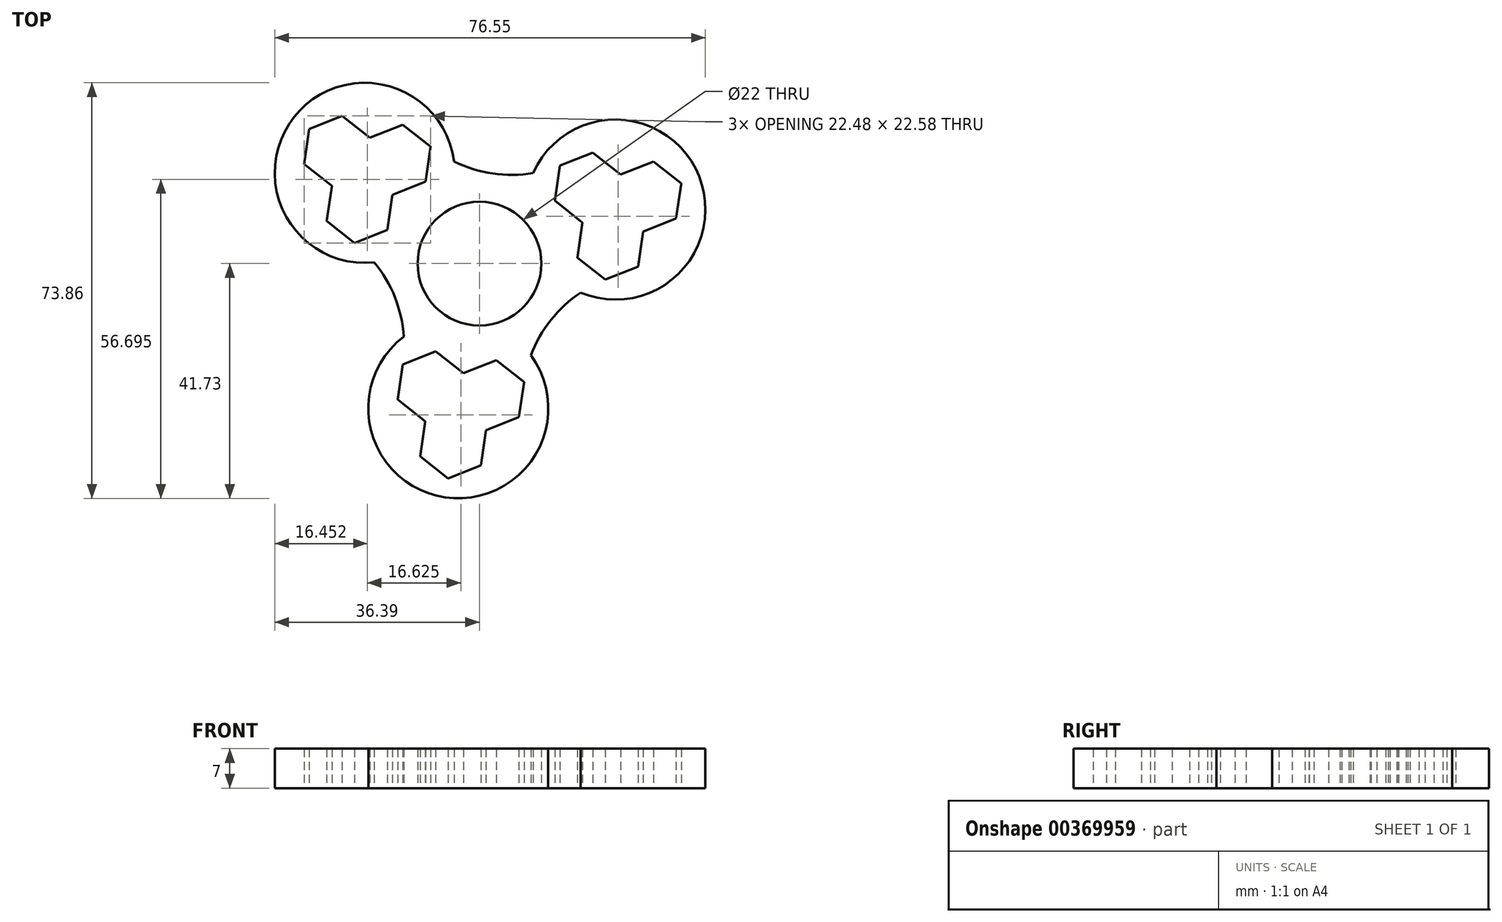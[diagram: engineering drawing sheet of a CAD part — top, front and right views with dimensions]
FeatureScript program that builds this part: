
annotation { "Feature Type Name" : "Feature", "Feature Type Description" : "" }
export const myFeature = defineFeature(function(context is Context, id is Id, definition is map)
    precondition{}
    {
        {
            var Q0;
            Q0=qCreatedBy(makeId("Top.planeOp"),FACE);
            var sketch = newSketch(context, id + "F0", { "sketchPlane" : qUnion([Q0])});
            skCircle(sketch, "E0", {"center": v(0, 0) * mm, "radius": 15 * mm});
            skCircle(sketch, "E1", {"center": v(0, 0) * mm, "radius": 11 * mm});
            skLineSegment(sketch, "E2", {"start": v(0, 0) * mm, "end": v(-20.4, 16.13) * mm});
            skLineSegment(sketch, "E3", {"start": v(0, 0) * mm, "end": v(24.16, 9.6) * mm});
            skLineSegment(sketch, "E4", {"start": v(0, 0) * mm, "end": v(-3.77, -25.73) * mm});
            skPoint(sketch, "E5.0.midPoint", {"position": v(-16.08, 12.72) * mm});
            skPoint(sketch, "E6.0.midPoint", {"position": v(19.05, 7.57) * mm});
            skPoint(sketch, "E7.0.midPoint", {"position": v(-2.97, -20.28) * mm});
            skCircle(sketch, "E8", {"center": v(-3.77, -25.73) * mm, "radius": 16 * mm});
            skCircle(sketch, "E9", {"center": v(-20.4, 16.13) * mm, "radius": 16 * mm});
            skCircle(sketch, "E10", {"center": v(24.16, 9.6) * mm, "radius": 16 * mm});
            skCircle(sketch, "E11.cCircle", {"center": v(-25.33, 20.03) * mm, "radius": 6.3 * mm, "construction": true});
            skLineSegment(sketch, "E11.0", {"start": v(-19.48, 22.35) * mm, "end": v(-20.4, 16.13) * mm});
            skLineSegment(sketch, "E11.1", {"start": v(-20.4, 16.13) * mm, "end": v(-26.24, 13.8) * mm});
            skLineSegment(sketch, "E11.2", {"start": v(-26.24, 13.8) * mm, "end": v(-31.18, 17.7) * mm});
            skLineSegment(sketch, "E11.3", {"start": v(-31.18, 17.7) * mm, "end": v(-30.27, 23.93) * mm});
            skLineSegment(sketch, "E11.4", {"start": v(-30.27, 23.93) * mm, "end": v(-24.42, 26.26) * mm});
            skLineSegment(sketch, "E11.5", {"start": v(-24.42, 26.26) * mm, "end": v(-19.48, 22.35) * mm});
            skCircle(sketch, "E12.cCircle", {"center": v(-14.55, 18.45) * mm, "radius": 6.3 * mm, "construction": true});
            skLineSegment(sketch, "E12.0", {"start": v(-8.7, 20.77) * mm, "end": v(-9.6, 14.55) * mm});
            skLineSegment(sketch, "E12.1", {"start": v(-9.6, 14.55) * mm, "end": v(-15.46, 12.22) * mm});
            skLineSegment(sketch, "E12.2", {"start": v(-15.46, 12.22) * mm, "end": v(-20.4, 16.13) * mm});
            skLineSegment(sketch, "E12.3", {"start": v(-20.4, 16.13) * mm, "end": v(-19.48, 22.35) * mm});
            skLineSegment(sketch, "E12.4", {"start": v(-19.48, 22.35) * mm, "end": v(-13.63, 24.68) * mm});
            skLineSegment(sketch, "E12.5", {"start": v(-13.63, 24.68) * mm, "end": v(-8.7, 20.77) * mm});
            skCircle(sketch, "E13.cCircle", {"center": v(-21.3, 9.9) * mm, "radius": 6.3 * mm, "construction": true});
            skLineSegment(sketch, "E13.0", {"start": v(-16.37, 6) * mm, "end": v(-22.22, 3.67) * mm});
            skLineSegment(sketch, "E13.1", {"start": v(-22.22, 3.67) * mm, "end": v(-27.16, 7.58) * mm});
            skLineSegment(sketch, "E13.2", {"start": v(-27.16, 7.58) * mm, "end": v(-26.24, 13.8) * mm});
            skLineSegment(sketch, "E13.3", {"start": v(-26.24, 13.8) * mm, "end": v(-20.4, 16.13) * mm});
            skLineSegment(sketch, "E13.4", {"start": v(-20.4, 16.13) * mm, "end": v(-15.46, 12.22) * mm});
            skLineSegment(sketch, "E13.5", {"start": v(-15.46, 12.22) * mm, "end": v(-16.37, 6) * mm});
            skCircle(sketch, "E14.MirrorC", {"center": v(30.01, 11.92) * mm, "radius": 6.3 * mm, "construction": true});
            skCircle(sketch, "E15.MirrorC", {"center": v(19.23, 13.5) * mm, "radius": 6.3 * mm, "construction": true});
            skCircle(sketch, "E16.MirrorC", {"center": v(23.25, 3.37) * mm, "radius": 6.3 * mm, "construction": true});
            skLineSegment(sketch, "E17.MirrorCS", {"start": v(30.92, 18.15) * mm, "end": v(25.08, 15.82) * mm});
            skLineSegment(sketch, "E18.MirrorCS", {"start": v(35.86, 14.24) * mm, "end": v(30.92, 18.15) * mm});
            skLineSegment(sketch, "E19.MirrorCS", {"start": v(34.95, 8.02) * mm, "end": v(35.86, 14.24) * mm});
            skLineSegment(sketch, "E20.MirrorCS", {"start": v(29.1, 5.7) * mm, "end": v(34.95, 8.02) * mm});
            skLineSegment(sketch, "E21.MirrorCS", {"start": v(24.16, 9.6) * mm, "end": v(29.1, 5.7) * mm});
            skLineSegment(sketch, "E22.MirrorCS", {"start": v(25.08, 15.82) * mm, "end": v(24.16, 9.6) * mm});
            skLineSegment(sketch, "E23.MirrorCS", {"start": v(25.08, 15.82) * mm, "end": v(20.14, 19.73) * mm});
            skLineSegment(sketch, "E24.MirrorCS", {"start": v(20.14, 19.73) * mm, "end": v(14.3, 17.4) * mm});
            skLineSegment(sketch, "E25.MirrorCS", {"start": v(14.3, 17.4) * mm, "end": v(13.38, 11.18) * mm});
            skLineSegment(sketch, "E26.MirrorCS", {"start": v(13.38, 11.18) * mm, "end": v(18.31, 7.28) * mm});
            skLineSegment(sketch, "E27.MirrorCS", {"start": v(18.31, 7.28) * mm, "end": v(24.16, 9.6) * mm});
            skLineSegment(sketch, "E28.MirrorCS", {"start": v(28.19, -0.53) * mm, "end": v(29.1, 5.7) * mm});
            skLineSegment(sketch, "E29.MirrorCS", {"start": v(22.34, -2.85) * mm, "end": v(28.19, -0.53) * mm});
            skLineSegment(sketch, "E30.MirrorCS", {"start": v(17.4, 1.05) * mm, "end": v(22.34, -2.85) * mm});
            skLineSegment(sketch, "E31.MirrorCS", {"start": v(18.31, 7.28) * mm, "end": v(17.4, 1.05) * mm});
            skLineSegment(sketch, "E32.MirrorCS", {"start": v(-14.55, -24.15) * mm, "end": v(-13.64, -17.92) * mm});
            skLineSegment(sketch, "E33.MirrorCS", {"start": v(-9.62, -28.05) * mm, "end": v(-14.55, -24.15) * mm});
            skLineSegment(sketch, "E34.MirrorCS", {"start": v(-13.64, -17.92) * mm, "end": v(-7.8, -15.6) * mm});
            skLineSegment(sketch, "E35.MirrorCS", {"start": v(-9.62, -28.05) * mm, "end": v(-3.77, -25.73) * mm});
            skLineSegment(sketch, "E36.MirrorCS", {"start": v(-10.53, -34.28) * mm, "end": v(-9.62, -28.05) * mm});
            skLineSegment(sketch, "E37.MirrorCS", {"start": v(-5.6, -38.18) * mm, "end": v(-10.53, -34.28) * mm});
            skLineSegment(sketch, "E38.MirrorCS", {"start": v(0.25, -35.86) * mm, "end": v(-5.6, -38.18) * mm});
            skLineSegment(sketch, "E39.MirrorCS", {"start": v(1.17, -29.63) * mm, "end": v(0.25, -35.86) * mm});
            skLineSegment(sketch, "E40.MirrorCS", {"start": v(-3.77, -25.73) * mm, "end": v(1.17, -29.63) * mm});
            skLineSegment(sketch, "E41.MirrorCS", {"start": v(-2.86, -19.5) * mm, "end": v(3, -17.18) * mm});
            skLineSegment(sketch, "E42.MirrorCS", {"start": v(7.02, -27.3) * mm, "end": v(1.17, -29.63) * mm});
            skLineSegment(sketch, "E43.MirrorCS", {"start": v(7.93, -21.08) * mm, "end": v(7.02, -27.3) * mm});
            skLineSegment(sketch, "E44.MirrorCS", {"start": v(3, -17.18) * mm, "end": v(7.93, -21.08) * mm});
            skLineSegment(sketch, "E45.MirrorCS", {"start": v(-7.8, -15.6) * mm, "end": v(-2.86, -19.5) * mm});
            skCircle(sketch, "E46.MirrorC", {"center": v(-8.7, -21.82) * mm, "radius": 6.3 * mm, "construction": true});
            skCircle(sketch, "E47.MirrorC", {"center": v(-4.68, -31.95) * mm, "radius": 6.3 * mm, "construction": true});
            skCircle(sketch, "E48.MirrorC", {"center": v(2.08, -23.4) * mm, "radius": 6.3 * mm, "construction": true});
            skLineSegment(sketch, "E49", {"start": v(-8.7, 20.77) * mm, "end": v(14.3, 17.4) * mm, "construction": true});
            skLineSegment(sketch, "E50", {"start": v(22.34, -2.85) * mm, "end": v(7.93, -21.08) * mm, "construction": true});
            skLineSegment(sketch, "E51", {"start": v(-13.64, -17.92) * mm, "end": v(-22.22, 3.67) * mm, "construction": true});
            skArc(sketch, "E52", {"start": v(-8.7, 20.77) * mm, "mid": v(2.35, 16) * mm, "end": v(14.3, 17.4) * mm});
            skArc(sketch, "E53", {"start": v(22.34, -2.85) * mm, "mid": v(12.7, -10.04) * mm, "end": v(7.93, -21.08) * mm});
            skArc(sketch, "E54", {"start": v(-13.64, -17.92) * mm, "mid": v(-15.04, -5.97) * mm, "end": v(-22.22, 3.67) * mm});
            skSolve(sketch);
        }
        {
            var Q0;
            Q0 = qSketchRegion(id + "F0", true);
            var Q1;
            {var subQ5=sQuery(id+"F0.wireOp",EDGE,"E10");var subQ6=sQuery(id+"F0.wireOp",EDGE,"E0");var subQ7=makeQuery(id+"F0.imprint","INTERSECT",VERTEX,{"disambiguationData":[OD(1.0)],"derivedFrom":[subQ6,subQ5]});Q1=makeQuery(id+"F0.imprint","IMPRINT",FACE,{"disambiguationData":[TD([[makeQuery(id+"F0.imprint","IMPRINT",EDGE,{"disambiguationData":[TD([[subQ7,-1.0]])],"derivedFrom":subQ6}),1.0]])]});}
            var Q2;
            {var subQ3=sQuery(id+"F0.wireOp",EDGE,"E10");var subQ6=sQuery(id+"F0.wireOp",EDGE,"E0");var subQ10=makeQuery(id+"F0.imprint","INTERSECT",VERTEX,{"disambiguationData":[OD(0.0)],"derivedFrom":[subQ6,subQ3]});Q2=makeQuery(id+"F0.imprint","IMPRINT",FACE,{"disambiguationData":[TD([[makeQuery(id+"F0.imprint","IMPRINT",EDGE,{"disambiguationData":[TD([[subQ10,1.0]])],"derivedFrom":subQ6}),1.0]])]});}
            var Q3;
            {var subQ1=sQuery(id+"F0.wireOp",EDGE,"E0");var subQ8=sQuery(id+"F0.wireOp",EDGE,"E9");var subQ11=makeQuery(id+"F0.imprint","INTERSECT",VERTEX,{"disambiguationData":[OD(1.0)],"derivedFrom":[subQ1,subQ8]});Q3=makeQuery(id+"F0.imprint","IMPRINT",FACE,{"disambiguationData":[TD([[makeQuery(id+"F0.imprint","IMPRINT",EDGE,{"disambiguationData":[TD([[subQ11,-1.0]])],"derivedFrom":subQ1}),1.0]])]});}
            var Q4;
            {var subQ0=sQuery(id+"F0.wireOp",EDGE,"E2");var subQ1=sQuery(id+"F0.wireOp",EDGE,"E0");var subQ2=makeQuery(id+"F0.imprint","INTERSECT",VERTEX,{"derivedFrom":[subQ1,subQ0]});Q4=makeQuery(id+"F0.imprint","IMPRINT",FACE,{"disambiguationData":[TD([[makeQuery(id+"F0.imprint","IMPRINT",EDGE,{"disambiguationData":[TD([[subQ2,-1.0]])],"derivedFrom":subQ1}),1.0]])]});}
            var Q5;
            {var subQ0=sQuery(id+"F0.wireOp",EDGE,"E9");var subQ1=sQuery(id+"F0.wireOp",EDGE,"E0");var subQ2=makeQuery(id+"F0.imprint","INTERSECT",VERTEX,{"disambiguationData":[OD(0.0)],"derivedFrom":[subQ1,subQ0]});Q5=makeQuery(id+"F0.imprint","IMPRINT",FACE,{"disambiguationData":[TD([[makeQuery(id+"F0.imprint","IMPRINT",EDGE,{"disambiguationData":[TD([[subQ2,-1.0]])],"derivedFrom":subQ1}),1.0]])]});}
            var Q6;
            {var subQ0=sQuery(id+"F0.wireOp",EDGE,"E3");var subQ1=sQuery(id+"F0.wireOp",EDGE,"E0");var subQ2=makeQuery(id+"F0.imprint","INTERSECT",VERTEX,{"derivedFrom":[subQ1,subQ0]});Q6=makeQuery(id+"F0.imprint","IMPRINT",FACE,{"disambiguationData":[TD([[makeQuery(id+"F0.imprint","IMPRINT",EDGE,{"disambiguationData":[TD([[subQ2,-1.0]])],"derivedFrom":subQ1}),1.0]])]});}
            var Q7;
            {var subQ0=sQuery(id+"F0.wireOp",EDGE,"E3");var subQ1=sQuery(id+"F0.wireOp",EDGE,"E0");var subQ2=makeQuery(id+"F0.imprint","INTERSECT",VERTEX,{"derivedFrom":[subQ1,subQ0]});Q7=makeQuery(id+"F0.imprint","IMPRINT",FACE,{"disambiguationData":[TD([[makeQuery(id+"F0.imprint","IMPRINT",EDGE,{"disambiguationData":[TD([[subQ2,1.0]])],"derivedFrom":subQ1}),1.0]])]});}
            var Q8;
            {var subQ0=sQuery(id+"F0.wireOp",EDGE,"E8");var subQ1=sQuery(id+"F0.wireOp",EDGE,"E0");var subQ2=makeQuery(id+"F0.imprint","INTERSECT",VERTEX,{"disambiguationData":[OD(0.0)],"derivedFrom":[subQ1,subQ0]});Q8=makeQuery(id+"F0.imprint","IMPRINT",FACE,{"disambiguationData":[TD([[makeQuery(id+"F0.imprint","IMPRINT",EDGE,{"disambiguationData":[TD([[subQ2,-1.0]])],"derivedFrom":subQ1}),1.0]])]});}
            var Q9;
            {var subQ0=sQuery(id+"F0.wireOp",EDGE,"E4");var subQ1=sQuery(id+"F0.wireOp",EDGE,"E0");var subQ2=makeQuery(id+"F0.imprint","INTERSECT",VERTEX,{"derivedFrom":[subQ1,subQ0]});Q9=makeQuery(id+"F0.imprint","IMPRINT",FACE,{"disambiguationData":[TD([[makeQuery(id+"F0.imprint","IMPRINT",EDGE,{"disambiguationData":[TD([[subQ2,-1.0]])],"derivedFrom":subQ1}),1.0]])]});}
            var Q10;
            {var subQ3=sQuery(id+"F0.wireOp",EDGE,"E10");var subQ6=sQuery(id+"F0.wireOp",EDGE,"E0");var subQ11=makeQuery(id+"F0.imprint","INTERSECT",VERTEX,{"disambiguationData":[OD(0.0)],"derivedFrom":[subQ6,subQ3]});Q10=makeQuery(id+"F0.imprint","IMPRINT",FACE,{"disambiguationData":[TD([[makeQuery(id+"F0.imprint","IMPRINT",EDGE,{"disambiguationData":[TD([[subQ11,-1.0]])],"derivedFrom":subQ6}),1.0]])]});}
            var Q11;
            {var subQ0=sQuery(id+"F0.wireOp",EDGE,"E8");var subQ1=sQuery(id+"F0.wireOp",EDGE,"E0");var subQ2=makeQuery(id+"F0.imprint","INTERSECT",VERTEX,{"disambiguationData":[OD(1.0)],"derivedFrom":[subQ1,subQ0]});Q11=makeQuery(id+"F0.imprint","IMPRINT",FACE,{"disambiguationData":[TD([[makeQuery(id+"F0.imprint","IMPRINT",EDGE,{"disambiguationData":[TD([[subQ2,-1.0]])],"derivedFrom":subQ1}),1.0]])]});}
            extrude(context, id + "F1", {"entities" : qUnion([Q0, Q1, Q2, Q3, Q4, Q5, Q6, Q7, Q8, Q9, Q10, Q11]), "depth" : 7 * mm});
        }
    });
